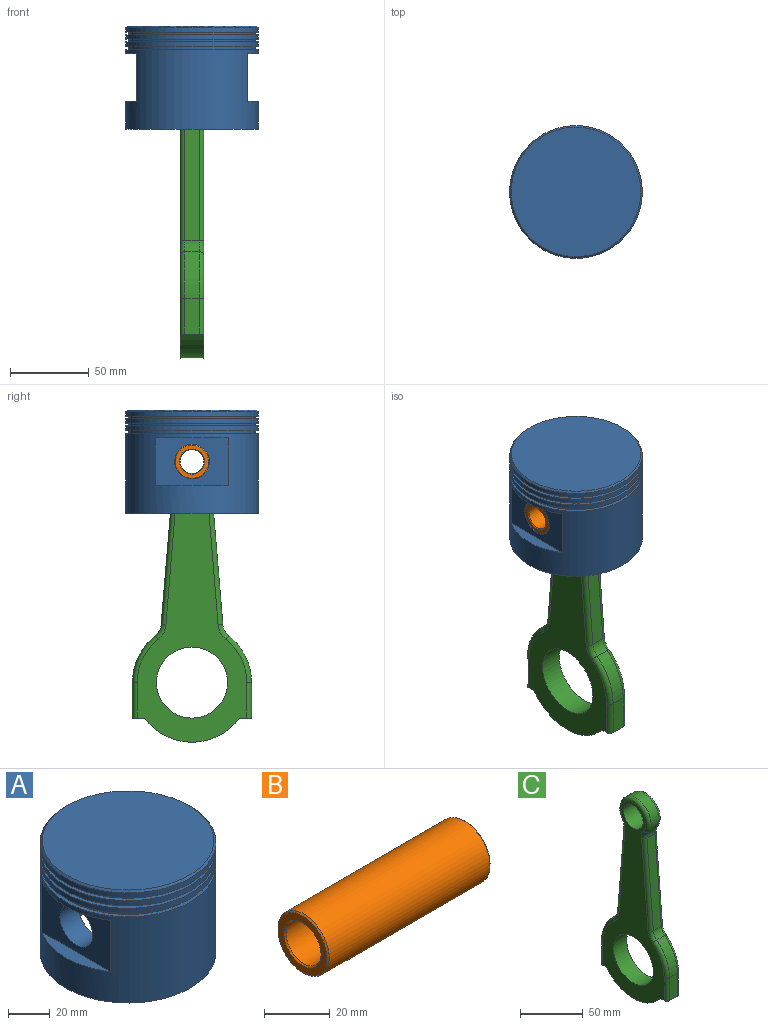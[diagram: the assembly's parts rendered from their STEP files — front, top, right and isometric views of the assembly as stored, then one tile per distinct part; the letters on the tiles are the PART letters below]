
ASSEMBLY  parts=3 mates=2
PART A: 29 faces, bbox 84x84x65.4 mm
  f0: cylinder r=42mm len=84mm, axis (0,0,-1), area 10348.4mm2, adj f14,f16,f23,f24,f25,f26,f27,f28
  f1: cylinder r=11mm len=22mm, axis (1,0,0), area 863.9mm2, adj f19,f25
  f2: cylinder r=42mm len=84mm, axis (0,0,-1), area 791.7mm2, adj f4,f5
  f3: plane 82x82mm, normal (0,0,1), area 5281mm2, adj f4
  f4: cone r=41mm half-angle=45deg, axis (0,0,-1), area 368.8mm2, adj f2,f3
  f5: plane 84x84mm, normal (0,0,-1), area 515.2mm2, adj f2,f7
  f6: plane 84x84mm, normal (0,0,1), area 515.2mm2, adj f7,f8
  f7: cylinder r=40mm len=80mm, axis (0,0,1), area 377mm2, adj f5,f6
  f8: cylinder r=42mm len=84mm, axis (0,0,-1), area 791.7mm2, adj f6,f9
  f9: plane 84x84mm, normal (0,0,-1), area 515.2mm2, adj f8,f11
  f10: plane 84x84mm, normal (0,0,1), area 515.2mm2, adj f11,f12
  f11: cylinder r=40mm len=80mm, axis (0,0,1), area 377mm2, adj f9,f10
  f12: cylinder r=42mm len=84mm, axis (0,0,-1), area 791.7mm2, adj f10,f13
  f13: plane 84x84mm, normal (0,0,-1), area 515.2mm2, adj f12,f15
  f14: plane 84x84mm, normal (0,0,1), area 515.2mm2, adj f0,f15
  f15: cylinder r=40mm len=80mm, axis (0,0,1), area 502.7mm2, adj f13,f14
  f16: plane 84x84mm, normal (0,0,-1), area 2333.7mm2, adj f0,f18,f19,f20,f21
  f17: plane 76x45mm, normal (0,0,-1), area 3208.1mm2, adj f18,f19,f20,f21
  f18: cylinder r=38mm len=60.4mm, axis (0,0,-1), area 2908.8mm2, adj f16,f17,f19,f20
  f19: plane 61.25x60.4mm, normal (1,0,0), area 3319.1mm2, adj f1,f16,f17,f18,f21
  f20: plane 61.25x60.4mm, normal (-1,0,0), area 3319.1mm2, adj f16,f17,f18,f21,f22
  f21: cylinder r=38mm len=60.4mm, axis (0,0,-1), area 2908.8mm2, adj f16,f17,f19,f20
  f22: cylinder r=11mm len=22mm, axis (1,0,0), area 863.9mm2, adj f20,f28
  f23: plane 46.43x7mm, normal (0,0,-1), area 220.6mm2, adj f0,f25
  f24: plane 46.43x7mm, normal (0,0,1), area 220.6mm2, adj f0,f25
  f25: plane 46.43x30mm, normal (-1,0,0), area 1012.8mm2, adj f0,f1,f23,f24
  f26: plane 46.43x7mm, normal (0,0,-1), area 220.6mm2, adj f0,f28
  f27: plane 46.43x7mm, normal (0,0,1), area 220.6mm2, adj f0,f28
  f28: plane 46.43x30mm, normal (1,0,0), area 1012.8mm2, adj f0,f22,f26,f27
PART B: 8 faces, bbox 70x22x22 mm
  f0: cylinder r=7.5mm len=69mm, axis (-1,0,0), area 3251.5mm2, adj f4,f6
  f1: cylinder r=11mm len=69mm, axis (-1,0,0), area 4768.9mm2, adj f5,f7
  f2: plane 21x21mm, normal (1,0,0), area 145.3mm2, adj f6,f7
  f3: plane 21x21mm, normal (-1,0,0), area 145.3mm2, adj f4,f5
  f4: cone r=8mm half-angle=45deg, axis (-1,0,0), area 34.4mm2, adj f0,f3
  f5: cone r=11mm half-angle=45deg, axis (1,0,0), area 47.8mm2, adj f1,f3
  f6: cone r=7.5mm half-angle=45deg, axis (1,0,0), area 34.4mm2, adj f0,f2
  f7: cone r=10.5mm half-angle=45deg, axis (-1,0,0), area 47.8mm2, adj f1,f2
PART C: 40 faces, bbox 15x81.7x196.1 mm
  f0: plane 87.32x9mm, normal (0,-1,0.08), area 788.5mm2, adj f14,f17,f21,f32
  f1: cylinder r=37.72mm len=29.64mm, axis (-1,0,0), area 306.9mm2, adj f2,f14,f19,f30
  f2: plane 22.5x9mm, normal (0,-1,0), area 202.5mm2, adj f1,f3,f18,f29
  f3: plane 15x7.45mm, normal (0,0,-1), area 107.8mm2, adj f2,f4,f12,f13,f18,f29
  f4: cylinder r=37.72mm len=60.56mm, axis (-1,0,0), area 1054.4mm2, adj f3,f5,f12,f13
  f5: plane 15x7.45mm, normal (0,0,-1), area 107.8mm2, adj f4,f6,f12,f13,f28,f39
  f6: plane 22.5x9mm, normal (0,1,0), area 202.5mm2, adj f5,f7,f28,f39
  f7: cylinder r=37.72mm len=29.64mm, axis (-1,0,0), area 306.9mm2, adj f6,f15,f27,f38
  f8: plane 87.32x9mm, normal (0,1,0.08), area 788.5mm2, adj f15,f16,f25,f36
  f9: cylinder r=11mm len=22mm, axis (-1,0,0), area 1036.7mm2, adj f12,f13
  f10: cylinder r=22.5mm len=45mm, axis (-1,0,0), area 2120.6mm2, adj f12,f13
  f11: cylinder r=17mm len=34mm, axis (-1,0,0), area 663.5mm2, adj f16,f17,f23,f34
  f12: plane 191.72x69.45mm, normal (1,0,0), area 5192.2mm2, adj f3,f4,f5,f9,f10,f29,f30,f31
  f13: plane 191.72x69.45mm, normal (-1,0,0), area 5192.2mm2, adj f3,f4,f5,f9,f10,f18,f19,f20
  f14: cylinder r=10mm len=9mm, axis (-1,0,0), area 73.9mm2, adj f0,f1,f20,f31
  f15: cylinder r=10mm len=9mm, axis (-1,0,0), area 73.9mm2, adj f7,f8,f26,f37
  f16: cylinder r=10mm len=9mm, axis (-1,0,0), area 61.2mm2, adj f8,f11,f24,f35
  f17: cylinder r=10mm len=9mm, axis (-1,0,0), area 61.2mm2, adj f0,f11,f22,f33
  f18: cylinder r=3mm len=22.5mm, axis (0,0,-1), area 106mm2, adj f2,f3,f13,f19
  f19: torus R=34.72mm, axis (1,0,0), area 156mm2, adj f1,f13,f18,f20
  f20: torus R=13mm, axis (1,0,0), area 42.9mm2, adj f13,f14,f19,f21
  f21: cylinder r=3mm len=87.56mm, axis (0,-0.08,-1), area 412.9mm2, adj f0,f13,f20,f22
  f22: torus R=13mm, axis (1,0,0), area 35.5mm2, adj f13,f17,f21,f23
  f23: torus R=14mm, axis (1,0,0), area 325.1mm2, adj f11,f13,f22,f24
  f24: torus R=13mm, axis (1,0,0), area 35.5mm2, adj f13,f16,f23,f25
  f25: cylinder r=3mm len=87.56mm, axis (0,-0.08,1), area 412.9mm2, adj f8,f13,f24,f26
  f26: torus R=13mm, axis (1,0,0), area 42.9mm2, adj f13,f15,f25,f27
  f27: torus R=34.72mm, axis (1,0,0), area 156mm2, adj f7,f13,f26,f28
  f28: cylinder r=3mm len=22.5mm, axis (0,0,1), area 106mm2, adj f5,f6,f13,f27
  f29: cylinder r=3mm len=22.5mm, axis (0,0,1), area 106mm2, adj f2,f3,f12,f30
  f30: torus R=34.72mm, axis (1,0,0), area 156mm2, adj f1,f12,f29,f31
  f31: torus R=13mm, axis (1,0,0), area 42.9mm2, adj f12,f14,f30,f32
  f32: cylinder r=3mm len=87.56mm, axis (0,0.08,1), area 412.9mm2, adj f0,f12,f31,f33
  f33: torus R=13mm, axis (1,0,0), area 35.5mm2, adj f12,f17,f32,f34
  f34: torus R=14mm, axis (1,0,0), area 325.1mm2, adj f11,f12,f33,f35
  f35: torus R=13mm, axis (1,0,0), area 35.5mm2, adj f12,f16,f34,f36
  f36: cylinder r=3mm len=87.56mm, axis (0,0.08,-1), area 412.9mm2, adj f8,f12,f35,f37
  f37: torus R=13mm, axis (1,0,0), area 42.9mm2, adj f12,f15,f36,f38
  f38: torus R=34.72mm, axis (1,0,0), area 156mm2, adj f7,f12,f37,f39
  f39: cylinder r=3mm len=22.5mm, axis (0,0,-1), area 106mm2, adj f5,f6,f12,f38
PLACE A at identity fixed
PLACE B at identity
PLACE C t=(0,0,-140)mm
MATE revolute C.f9 <-> B.f1  axis (-1,0,0) through (0,0,0)mm
MATE fastened B.f1 <-> A.f1  axis (1,0,0) through (35,0,0)mm
